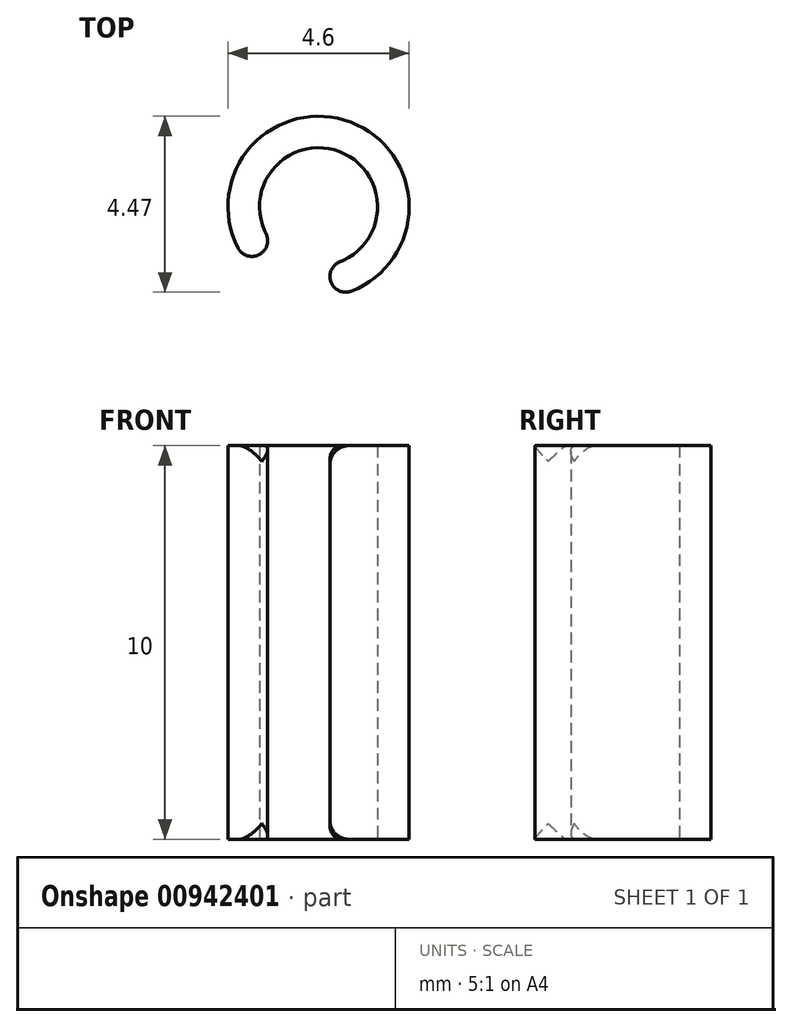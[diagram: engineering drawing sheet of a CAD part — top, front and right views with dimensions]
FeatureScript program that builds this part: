
annotation { "Feature Type Name" : "Feature", "Feature Type Description" : "" }
export const myFeature = defineFeature(function(context is Context, id is Id, definition is map)
    precondition{}
    {
        {
            var Q0;
            Q0=qCreatedBy(makeId("Top.planeOp"),FACE);
            var sketch = newSketch(context, id + "F0", { "sketchPlane" : qUnion([Q0])});
            skCircle(sketch, "E0", {"center": v(0, 0) * mm, "radius": 1.5 * mm});
            skCircle(sketch, "E1", {"center": v(0, 0) * mm, "radius": 2.3 * mm});
            skLineSegment(sketch, "E2", {"start": v(0, 0) * mm, "end": v(-1.78, -1.45) * mm});
            skLineSegment(sketch, "E3", {"start": v(0, 0) * mm, "end": v(0.36, -2.27) * mm});
            skSolve(sketch);
        }
        {
            var Q0;
            {var subQ0=sQuery(id+"F0.wireOp",EDGE,"E2");var subQ1=sQuery(id+"F0.wireOp",EDGE,"E0");var subQ2=makeQuery(id+"F0.imprint","INTERSECT",VERTEX,{"derivedFrom":[subQ1,subQ0]});Q0=makeQuery(id+"F0.imprint","IMPRINT",FACE,{"disambiguationData":[TD([[makeQuery(id+"F0.imprint","IMPRINT",EDGE,{"disambiguationData":[TD([[subQ2,1.0]])],"derivedFrom":subQ1}),-1.0]])]});}
            extrude(context, id + "F1", {"entities" : qUnion([Q0]), "depth" : 10 * mm, "offsetDistance" : 25 * mm});
        }
        {
            var Q0;
            Q0=makeQuery(id+"F1.opExtrude","SWEPT_FACE",FACE,{"disambiguationData":[OSD([sQuery(id+"F0.wireOp",EDGE,"E2")])]});
            var Q1;
            Q1=makeQuery(id+"F1.opExtrude","SWEPT_FACE",FACE,{"disambiguationData":[OSD([sQuery(id+"F0.wireOp",EDGE,"E3")])]});
            fillet(context, id + "F2", {"entities" : qUnion([Q0, Q1]), "radius" : 0.4 * mm, "tangentPropagation" : true, "allowEdgeOverflow" : false});
        }
    });
